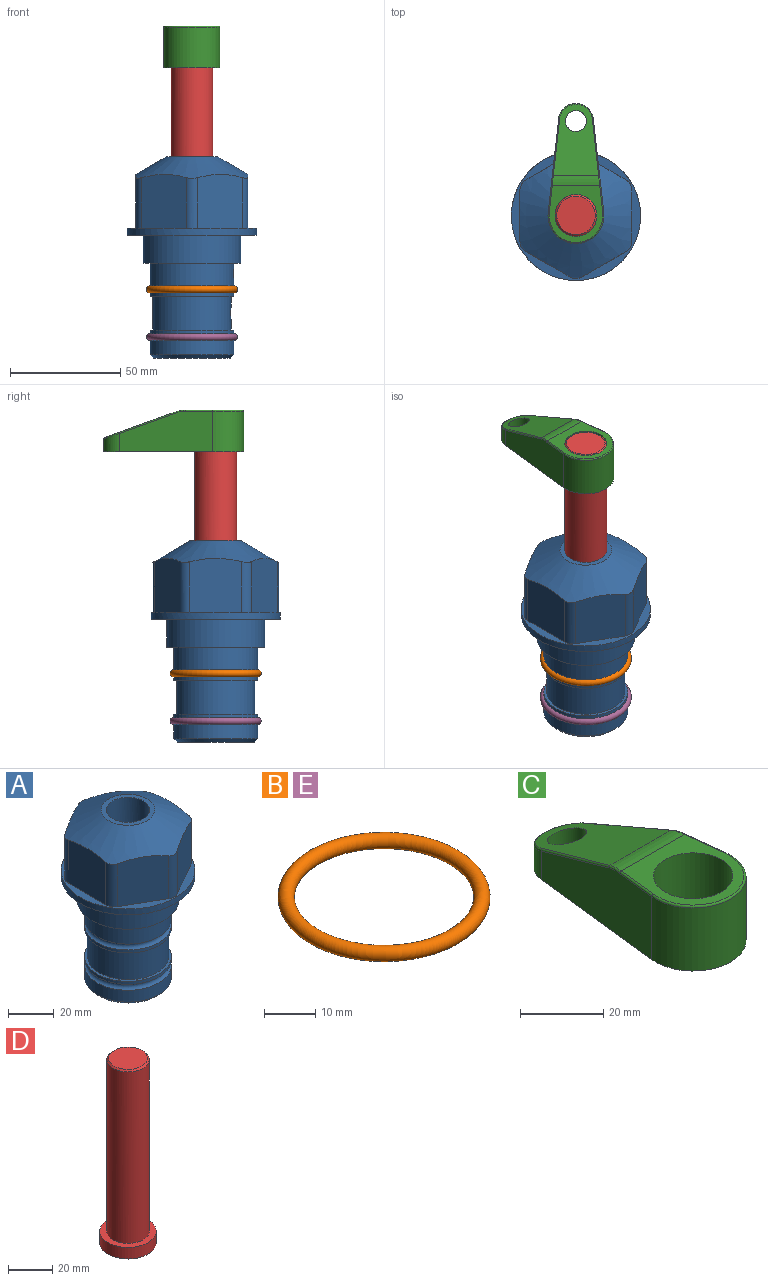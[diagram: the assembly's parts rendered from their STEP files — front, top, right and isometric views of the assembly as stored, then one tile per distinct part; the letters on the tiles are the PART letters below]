
ASSEMBLY  parts=5 mates=3
PART A: 36 faces, bbox 58.7x58.7x91.2 mm
  f0: cylinder r=17.78mm len=35.56mm, axis (0,0,1), area 1670.8mm2, adj f23,f24,f31
  f1: cylinder r=19.05mm len=38.1mm, axis (0,0,1), area 1191.9mm2, adj f26,f27,f30
  f2: plane 58.66x58.66mm, normal (0,0,-1), area 1150.6mm2, adj f3,f28
  f3: cylinder r=29.33mm len=58.66mm, axis (0,0,-1), area 585.1mm2, adj f2,f4
  f4: plane 58.66x58.66mm, normal (0,0,1), area 475.9mm2, adj f3,f5,f6,f7,f8,f9,f10,f11
  f5: plane 24.5x20.32mm, normal (-0.5,0.87,0), area 562.8mm2, adj f4,f15,f16,f17
  f6: plane 24.5x20.32mm, normal (0.5,0.87,0), area 562.8mm2, adj f4,f14,f15,f17
  f7: plane 24.5x23.48mm, normal (1,0,0), area 562.8mm2, adj f4,f13,f14,f17
  f8: plane 24.5x20.32mm, normal (0.5,-0.87,0), area 562.8mm2, adj f4,f12,f13,f17
  f9: plane 24.5x20.32mm, normal (-0.5,-0.87,0), area 562.8mm2, adj f4,f11,f12,f17
  f10: plane 24.5x23.48mm, normal (-1,0,0), area 562.8mm2, adj f4,f11,f16,f17
  f11: cylinder r=5.08mm len=23.01mm, axis (0,0,-1), area 121.2mm2, adj f4,f9,f10,f17
  f12: cylinder r=5.08mm len=23.01mm, axis (0,0,-1), area 121.2mm2, adj f4,f8,f9,f17
  f13: cylinder r=5.08mm len=23.01mm, axis (0,0,-1), area 121.2mm2, adj f4,f7,f8,f17
  f14: cylinder r=5.08mm len=23.01mm, axis (0,0,-1), area 121.2mm2, adj f4,f6,f7,f17
  f15: cylinder r=5.08mm len=23.01mm, axis (0,0,-1), area 121.2mm2, adj f4,f5,f6,f17
  f16: cylinder r=5.08mm len=23.01mm, axis (0,0,-1), area 121.2mm2, adj f4,f5,f10,f17
  f17: cone r=11.73mm half-angle=60deg, axis (0,0,-1), area 2071.8mm2, adj f5,f6,f7,f8,f9,f10,f11,f12
  f18: plane 23.46x23.46mm, normal (0,0,1), area 147.4mm2, adj f17,f35
  f19: plane 34.93x34.93mm, normal (0,0,-1), area 958mm2, adj f29
  f20: cylinder r=19.05mm len=38.1mm, axis (0,0,1), area 760.1mm2, adj f21,f29
  f21: torus R=19.05mm, axis (0,0,1), area 565.3mm2, adj f20,f22
  f22: cylinder r=19.05mm len=38.1mm, axis (0,0,1), area 190mm2, adj f21,f23
  f23: plane 38.1x38.1mm, normal (0,0,1), area 146.9mm2, adj f0,f22
  f24: plane 38.1x38.1mm, normal (0,0,-1), area 146.9mm2, adj f0,f25
  f25: cylinder r=19.05mm len=38.1mm, axis (0,0,1), area 190mm2, adj f24,f26
  f26: torus R=19.05mm, axis (0,0,1), area 565.3mm2, adj f1,f25
  f27: plane 44.45x44.45mm, normal (0,0,-1), area 411.7mm2, adj f1,f28
  f28: cylinder r=22.23mm len=44.45mm, axis (0,0,1), area 1773.5mm2, adj f2,f27
  f29: cone r=19.05mm half-angle=45deg, axis (0,0,1), area 257.5mm2, adj f19,f20
  f30: cylinder r=3.17mm len=6.75mm, axis (-1,0,0), area 128mm2, adj f1,f33
  f31: cylinder r=3.17mm len=6.35mm, axis (-1,0,0), area 102.5mm2, adj f0,f33
  f32: plane 25.4x25.4mm, normal (0,0,1), area 506.7mm2, adj f33
  f33: cylinder r=12.7mm len=66.42mm, axis (0,0,-1), area 5236.2mm2, adj f30,f31,f32,f34
  f34: cone r=9.53mm half-angle=30deg, axis (0,0,-1), area 443.4mm2, adj f33,f35
  f35: cylinder r=9.53mm len=19.05mm, axis (0,0,-1), area 849mm2, adj f18,f34
PART B: 1 faces, bbox 44.7x44.7x3.2 mm
  f0: torus R=19.05mm, axis (0,0,1), area 1193.9mm2
PART C: 44 faces, bbox 27.5x64.5x19.1 mm
  f0: plane 2.3x0.95mm, normal (0,0,-1), area 1mm2, adj f25,f30,f34
  f1: plane 63.5x25.4mm, normal (0,0,-1), area 561.7mm2, adj f2,f3,f4,f5,f6,f7,f19,f20
  f2: cylinder r=12.7mm len=25.4mm, axis (0,0,-1), area 792.2mm2, adj f1,f3,f5,f13
  f3: plane 42.33x18.54mm, normal (0.99,0.11,0), area 647mm2, adj f1,f2,f4,f11,f12,f14
  f4: cylinder r=7.94mm len=15.78mm, axis (0,0,-1), area 158.6mm2, adj f1,f3,f5,f16
  f5: plane 42.33x18.54mm, normal (-0.99,0.11,0), area 647mm2, adj f1,f2,f4,f15,f17,f18
  f6: cylinder r=9.53mm len=19.05mm, axis (0,0,-1), area 1140.1mm2, adj f1,f8
  f7: cylinder r=4.76mm len=10.98mm, axis (0,0,-1), area 276.1mm2, adj f1,f9
  f8: plane 25.83x24.38mm, normal (0,0,1), area 262.2mm2, adj f6,f10,f11,f13,f15
  f9: plane 32.49x20.55mm, normal (0,0.34,0.94), area 489.9mm2, adj f7,f10,f14,f16,f18
  f10: cylinder r=12.7mm len=21.49mm, axis (-1,0,0), area 93.2mm2, adj f8,f9,f12,f17
  f11: cylinder r=0.51mm len=12.34mm, axis (0.11,-0.99,0), area 9.9mm2, adj f3,f8,f12,f13
  f12: bspline ~7.62x1.64mm, area 3.5mm2, adj f3,f10,f11,f14
  f13: torus R=12.19mm, axis (0,0,1), area 33.6mm2, adj f2,f8,f11,f15
  f14: cylinder r=0.51mm len=26.01mm, axis (0.1,-0.93,0.34), area 21.6mm2, adj f3,f9,f12,f16
  f15: cylinder r=0.51mm len=12.34mm, axis (0.11,0.99,0), area 9.9mm2, adj f5,f8,f13,f17
  f16: bspline ~15.78x7.05mm, area 15.7mm2, adj f4,f9,f14,f18
  f17: bspline ~7.62x1.64mm, area 3.5mm2, adj f5,f10,f15,f18
  f18: cylinder r=0.51mm len=26.01mm, axis (0.1,0.93,-0.34), area 21.6mm2, adj f5,f9,f16,f17
  f19: plane 21.6x14.29mm, normal (-0.99,-0.11,0), area 242.6mm2, adj f1,f26,f28,f34,f36,f38
  f20: plane 21.6x14.29mm, normal (0.99,-0.11,0), area 242.6mm2, adj f1,f27,f29,f37,f39,f41
  f21: cylinder r=12.7mm len=14.29mm, axis (0,0,-1), area 173.2mm2, adj f1,f26,f27,f30,f31,f33
  f22: cylinder r=7.94mm len=7.63mm, axis (0,0,-1), area 53.8mm2, adj f1,f28,f29,f42
  f23: plane 2.3x0.95mm, normal (0,0,-1), area 1mm2, adj f25,f33,f37
  f24: plane 17.94x12.32mm, normal (0,-0.34,-0.94), area 191.2mm2, adj f25,f38,f41,f42
  f25: cylinder r=9.53mm len=12.93mm, axis (-1,0,0), area 37.5mm2, adj f0,f23,f24,f31,f36,f39
  f26: cylinder r=1.59mm len=14.29mm, axis (0,0,-1), area 49mm2, adj f1,f19,f21,f32
  f27: cylinder r=1.59mm len=14.29mm, axis (0,0,-1), area 49mm2, adj f1,f20,f21,f35
  f28: cylinder r=1.59mm len=7.28mm, axis (0,0,-1), area 22.1mm2, adj f1,f19,f22,f40
  f29: cylinder r=1.59mm len=7.28mm, axis (0,0,-1), area 22.1mm2, adj f1,f20,f22,f43
  f30: torus R=14.29mm, axis (0,0,1), area 5.8mm2, adj f0,f21,f31,f32
  f31: bspline ~11.06x2.73mm, area 20.8mm2, adj f21,f25,f30,f33
  f32: sphere r=1.59mm, area 5.4mm2, adj f26,f30,f34
  f33: torus R=14.29mm, axis (0,0,1), area 5.8mm2, adj f21,f23,f31,f35
  f34: cylinder r=1.59mm len=1.68mm, axis (-0.11,0.99,0), area 2.4mm2, adj f0,f19,f32,f36
  f35: sphere r=1.59mm, area 5.4mm2, adj f27,f33,f37
  f36: bspline ~5.82x2.33mm, area 7.7mm2, adj f19,f25,f34,f38
  f37: cylinder r=1.59mm len=1.68mm, axis (0.11,0.99,0), area 2.4mm2, adj f20,f23,f35,f39
  f38: cylinder r=1.59mm len=18.33mm, axis (0.1,-0.93,0.34), area 46.7mm2, adj f19,f24,f36,f40
  f39: bspline ~5.82x2.33mm, area 7.7mm2, adj f20,f25,f37,f41
  f40: sphere r=1.59mm, area 3.6mm2, adj f28,f38,f42
  f41: cylinder r=1.59mm len=18.33mm, axis (0.1,0.93,-0.34), area 46.7mm2, adj f20,f24,f39,f43
  f42: bspline ~8.31x1.84mm, area 15.3mm2, adj f22,f24,f40,f43
  f43: sphere r=1.59mm, area 3.6mm2, adj f29,f41,f42
PART D: 6 faces, bbox 25.4x25.4x101.6 mm
  f0: plane 17.46x17.46mm, normal (0,0,1), area 239.5mm2, adj f5
  f1: plane 25.4x25.4mm, normal (0,0,-1), area 506.7mm2, adj f2
  f2: cylinder r=12.7mm len=25.4mm, axis (0,0,1), area 506.7mm2, adj f1,f3
  f3: plane 25.4x25.4mm, normal (0,0,1), area 221.7mm2, adj f2,f4
  f4: cylinder r=9.53mm len=94.46mm, axis (0,0,1), area 5653mm2, adj f3,f5
  f5: cone r=8.73mm half-angle=45deg, axis (0,0,-1), area 64.4mm2, adj f0,f4
PART E: same geometry as B
PLACE A t=(46.33,29.98,5.87)mm
PLACE B t=(46.33,29.98,5.87)mm
PLACE C t=(46.33,29.98,81.78)mm
PLACE D t=(46.33,29.98,27.17)mm
PLACE E rot(axis=(1,0,0),180deg) t=(46.33,29.98,-64.74)mm
MATE fastened E.f0 <-> A.f0  axis (0,0,-1) through (46.33,29.98,-40.23)mm
MATE cylindrical D.f2 <-> A.f0  axis (0,0,1) through (46.33,29.98,52.81)mm
MATE fastened C.f2 <-> D.f2  axis (0,0,-1) through (46.33,29.98,100.83)mm
